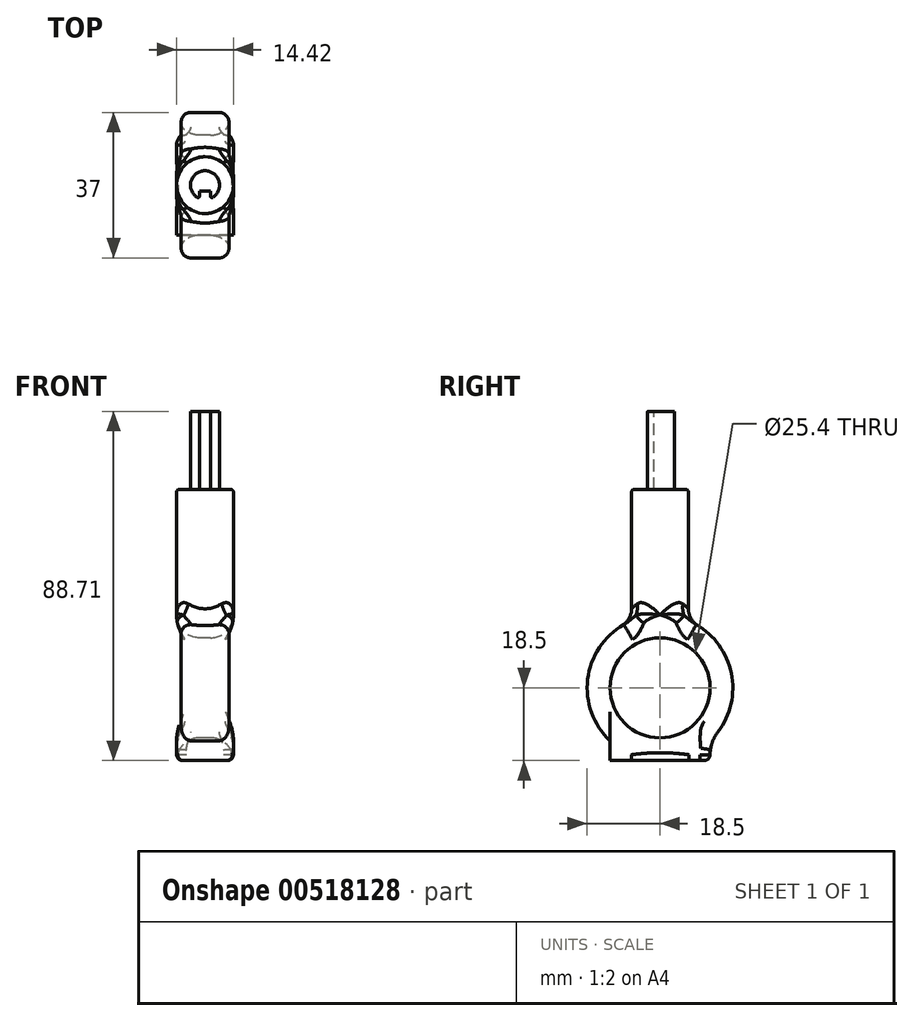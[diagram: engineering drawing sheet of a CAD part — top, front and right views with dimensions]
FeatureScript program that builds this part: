
annotation { "Feature Type Name" : "Feature", "Feature Type Description" : "" }
export const myFeature = defineFeature(function(context is Context, id is Id, definition is map)
    precondition{}
    {
        {
            var Q0;
            Q0=qCreatedBy(makeId("Top.planeOp"),FACE);
            var sketch = newSketch(context, id + "F0", { "sketchPlane" : qUnion([Q0])});
            skCircle(sketch, "E0", {"center": v(0, 0) * mm, "radius": 3.68 * mm});
            skSolve(sketch);
        }
        {
            var Q0;
            Q0 = qSketchRegion(id + "F0", true);
            extrude(context, id + "F1", {"entities" : qUnion([Q0]), "depth" : 19.8 * mm, "offsetDistance" : 25.4 * mm});
        }
        {
            var Q0;
            Q0=makeQuery(id+"F1.opExtrude","CAP_FACE",FACE,{"disambiguationData":[OSD([sQuery(id+"F0.wireOp",EDGE,"E0")])],"isStart":false});
            var sketch = newSketch(context, id + "F2", { "sketchPlane" : qUnion([Q0])});
            skLineSegment(sketch, "E1.bottom", {"start": v(-1.4, -3.68) * mm, "end": v(1.4, -3.68) * mm});
            skLineSegment(sketch, "E1.top", {"start": v(-1.4, -1.51) * mm, "end": v(1.4, -1.51) * mm});
            skLineSegment(sketch, "E1.left", {"start": v(-1.4, -3.68) * mm, "end": v(-1.4, -1.51) * mm});
            skLineSegment(sketch, "E1.right", {"start": v(1.4, -3.68) * mm, "end": v(1.4, -1.51) * mm});
            skSolve(sketch);
        }
        {
            var Q0;
            Q0 = qSketchRegion(id + "F2", true);
            extrude(context, id + "F3", {"entities" : qUnion([Q0]), "operationType" : NewBodyOperationType.REMOVE, "oppositeDirection" : true, "depth" : 25.4 * mm, "offsetDistance" : 25.4 * mm});
        }
        {
            var Q0;
            Q0=makeQuery(id+"F3.boolean.opBoolean","INTERSECT",EDGE,{"derivedFrom":[makeQuery(id+"F1.opExtrude","SWEPT_FACE",FACE,{"disambiguationData":[OSD([sQuery(id+"F0.wireOp",EDGE,"E0")])]}),makeQuery(id+"F3.opExtrude","SWEPT_FACE",FACE,{"disambiguationData":[OSD([sQuery(id+"F2.wireOp",EDGE,"E1.right")])]})]});
            var Q1;
            Q1=makeQuery(id+"F3.boolean.opBoolean","INTERSECT",EDGE,{"derivedFrom":[makeQuery(id+"F1.opExtrude","SWEPT_FACE",FACE,{"disambiguationData":[OSD([sQuery(id+"F0.wireOp",EDGE,"E0")])]}),makeQuery(id+"F3.opExtrude","SWEPT_FACE",FACE,{"disambiguationData":[OSD([sQuery(id+"F2.wireOp",EDGE,"E1.left")])]})]});
            fillet(context, id + "F4", {"entities" : qUnion([Q0, Q1]), "radius" : 0.38 * mm, "tangentPropagation" : true, "allowEdgeOverflow" : false});
        }
        {
            var Q0;
            Q0=makeQuery(id+"F1.opExtrude","CAP_FACE",FACE,{"disambiguationData":[OSD([sQuery(id+"F0.wireOp",EDGE,"E0")])],"isStart":true});
            var sketch = newSketch(context, id + "F5", { "sketchPlane" : qUnion([Q0])});
            skCircle(sketch, "E2", {"center": v(0, 0) * mm, "radius": 7.21 * mm});
            skSolve(sketch);
        }
        {
            var Q0;
            Q0 = qSketchRegion(id + "F5", true);
            extrude(context, id + "F6", {"entities" : qUnion([Q0]), "operationType" : NewBodyOperationType.ADD, "depth" : 12.7 * mm, "offsetDistance" : 25.4 * mm});
        }
        {
            var Q0;
            Q0=makeQuery(id+"F6.opExtrude","CAP_EDGE",EDGE,{"disambiguationData":[OSD([sQuery(id+"F5.wireOp",EDGE,"E2")])],"isStart":false});
            fillet(context, id + "F7", {"entities" : qUnion([Q0]), "radius" : 2.54 * mm, "tangentPropagation" : true, "allowEdgeOverflow" : false});
        }
        {
            var Q0;
            Q0=makeQuery(id+"F6.opExtrude","CAP_EDGE",EDGE,{"disambiguationData":[OSD([sQuery(id+"F5.wireOp",EDGE,"E2")])],"isStart":true});
            fillet(context, id + "F8", {"entities" : qUnion([Q0]), "radius" : 0.64 * mm, "tangentPropagation" : true, "allowEdgeOverflow" : false});
        }
        {
            var Q0;
            Q0=makeQuery(id+"F6.opExtrude","CAP_FACE",FACE,{"disambiguationData":[OSD([sQuery(id+"F5.wireOp",EDGE,"E2")])],"isStart":false});
            var sketch = newSketch(context, id + "F9", { "sketchPlane" : qUnion([Q0])});
            skCircle(sketch, "E3.0", {"center": v(0, 0) * mm, "radius": 7.21 * mm});
            skSolve(sketch);
        }
        {
            var Q0;
            Q0 = qSketchRegion(id + "F9", true);
            extrude(context, id + "F10", {"entities" : qUnion([Q0]), "operationType" : NewBodyOperationType.ADD, "depth" : 25 * mm, "offsetDistance" : 25 * mm, "hasSecondDirection" : true, "secondDirectionOppositeDirection" : true, "secondDirectionDepth" : 5 * mm});
        }
        {
            var Q0;
            Q0=qCreatedBy(makeId("Right.planeOp"),FACE);
            var sketch = newSketch(context, id + "F11", { "sketchPlane" : qUnion([Q0])});
            skCircle(sketch, "E4", {"center": v(0, -50.4) * mm, "radius": 12.7 * mm});
            skCircle(sketch, "E5", {"center": v(0, -50.4) * mm, "radius": 18.5 * mm});
            skSolve(sketch);
        }
        {
            var Q0;
            Q0 = qSketchRegion(id + "F11", true);
            extrude(context, id + "F12", {"entities" : qUnion([Q0]), "operationType" : NewBodyOperationType.ADD, "depth" : (14.43 / 2) * mm, "offsetDistance" : 25 * mm, "hasSecondDirection" : true, "secondDirectionOppositeDirection" : true, "secondDirectionDepth" : (14.43 / 2) * mm});
        }
        {
            var Q0;
            Q0=makeQuery(id+"F12.opExtrude","CAP_FACE",FACE,{"disambiguationData":[OSD([sQuery(id+"F11.wireOp",EDGE,"E4"),sQuery(id+"F11.wireOp",EDGE,"E5")])],"isStart":false});
            var sketch = newSketch(context, id + "F13", { "sketchPlane" : qUnion([Q0])});
            skLineSegment(sketch, "E6", {"start": v(-12.7, -63.85) * mm, "end": v(-12.7, -68.9) * mm});
            skLineSegment(sketch, "E7", {"start": v(-12.7, -68.9) * mm, "end": v(12.7, -68.9) * mm});
            skLineSegment(sketch, "E8", {"start": v(12.7, -68.9) * mm, "end": v(12.7, -63.85) * mm});
            skLineSegment(sketch, "E9", {"start": v(12.7, -63.85) * mm, "end": v(5.8, -66.43) * mm});
            skLineSegment(sketch, "E10", {"start": v(5.8, -66.43) * mm, "end": v(-3.07, -66.43) * mm});
            skLineSegment(sketch, "E11", {"start": v(-3.07, -66.43) * mm, "end": v(-12.7, -63.85) * mm});
            skSolve(sketch);
        }
        {
            var Q0;
            Q0 = qSketchRegion(id + "F13", true);
            var Q1;
            Q1=makeQuery(id+"F12.opExtrude","CAP_FACE",FACE,{"disambiguationData":[OSD([sQuery(id+"F11.wireOp",EDGE,"E4"),sQuery(id+"F11.wireOp",EDGE,"E5")])],"isStart":true});
            extrude(context, id + "F14", {"entities" : qUnion([Q0]), "operationType" : NewBodyOperationType.ADD, "endBound" : BoundingType.UP_TO_SURFACE, "oppositeDirection" : true, "depth" : 14.43 * mm, "endBoundEntityFace" : qUnion([Q1]), "offsetDistance" : 25 * mm});
        }
        {
            var Q0;
            Q0=makeQuery(id+"F14.opExtrude","SWEPT_EDGE",EDGE,{"disambiguationData":[OSD([sQuery(id+"F11.wireOp",EDGE,"E5"),sQuery(id+"F13.wireOp",EDGE,"E8"),sQuery(id+"F13.wireOp",EDGE,"E9")])]});
            var Q1;
            Q1=makeQuery(id+"F14.opExtrude","SWEPT_EDGE",EDGE,{"disambiguationData":[OSD([sQuery(id+"F11.wireOp",EDGE,"E5"),sQuery(id+"F13.wireOp",EDGE,"E6"),sQuery(id+"F13.wireOp",EDGE,"E11")])]});
            fillet(context, id + "F15", {"entities" : qUnion([Q0, Q1]), "tangentPropagation" : true, "radius" : 10 * mm, "defaultsChanged" : true, "vertexSettings" : [], "allowEdgeOverflow" : false});
        }
        {
            var Q0;
            Q0=makeQuery(id+"F12.opExtrude","CAP_EDGE",EDGE,{"disambiguationData":[OSD([sQuery(id+"F11.wireOp",EDGE,"E4")])],"isStart":false});
            fillet(context, id + "F16", {"entities" : qUnion([Q0]), "tangentPropagation" : true, "radius" : 5.8 * mm, "defaultsChanged" : true, "vertexSettings" : [], "allowEdgeOverflow" : false});
        }
        {
            var Q0;
            Q0=makeQuery(id+"F12.opExtrude","CAP_EDGE",EDGE,{"disambiguationData":[OSD([sQuery(id+"F11.wireOp",EDGE,"E4")])],"isStart":true});
            fillet(context, id + "F17", {"entities" : qUnion([Q0]), "tangentPropagation" : true, "radius" : 5.8 * mm, "defaultsChanged" : true, "vertexSettings" : [], "allowEdgeOverflow" : false});
        }
        {
            var Q0;
            Q0=makeQuery(id+"F12.boolean.opBoolean","INTERSECT",EDGE,{"disambiguationData":[OD(0.0)],"derivedFrom":[makeQuery(id+"F10.boolean.opBoolean","MERGE",FACE,{"derivedFrom":[makeQuery(id+"F6.opExtrude","SWEPT_FACE",FACE,{"disambiguationData":[OSD([sQuery(id+"F5.wireOp",EDGE,"E2")])]}),makeQuery(id+"F10.opExtrude","SWEPT_FACE",FACE,{"disambiguationData":[OSD([sQuery(id+"F9.wireOp",EDGE,"E3.0")])]})]}),makeQuery(id+"F12.opExtrude","SWEPT_FACE",FACE,{"disambiguationData":[OSD([sQuery(id+"F11.wireOp",EDGE,"E5")])]})]});
            fillet(context, id + "F18", {"entities" : qUnion([Q0]), "tangentPropagation" : true, "radius" : 5 * mm, "defaultsChanged" : false, "vertexSettings" : [], "allowEdgeOverflow" : false});
        }
        {
            var Q0;
            {var subQ0=sQuery(id+"F11.wireOp",EDGE,"E5");var subQ1=sQuery(id+"F11.wireOp",EDGE,"E4");var subQ7=sQuery(id+"F13.wireOp",EDGE,"E6");var subQ8=makeQuery(id+"F12.opExtrude","SWEPT_FACE",FACE,{"disambiguationData":[OSD([subQ0])]});Q0=makeQuery(id+"F16.opFillet","BLEND_EDGE",EDGE,{"blendedFrom":[makeQuery(id+"F12.opExtrude","CAP_EDGE",EDGE,{"disambiguationData":[OSD([subQ1])],"isStart":false}),makeQuery(id+"F14.boolean.opBoolean","SPLIT",FACE,{"disambiguationData":[TD([makeQuery(id+"F14.opExtrude","SWEPT_FACE",FACE,{"disambiguationData":[OSD([subQ7])]})])],"derivedFrom":subQ8})],"blendedInto":[makeQuery(id+"F14.boolean.opBoolean","SPLIT",FACE,{"disambiguationData":[TD([makeQuery(id+"F14.opExtrude","SWEPT_FACE",FACE,{"disambiguationData":[OSD([subQ7])]})])],"derivedFrom":subQ8})]});}
            var Q1;
            {var subQ0=sQuery(id+"F11.wireOp",EDGE,"E5");var subQ1=sQuery(id+"F11.wireOp",EDGE,"E4");var subQ5=sQuery(id+"F13.wireOp",EDGE,"E8");var subQ8=makeQuery(id+"F12.opExtrude","SWEPT_FACE",FACE,{"disambiguationData":[OSD([subQ0])]});Q1=makeQuery(id+"F16.opFillet","BLEND_EDGE",EDGE,{"blendedFrom":[makeQuery(id+"F12.opExtrude","CAP_EDGE",EDGE,{"disambiguationData":[OSD([subQ1])],"isStart":false}),makeQuery(id+"F14.boolean.opBoolean","SPLIT",FACE,{"disambiguationData":[TD([makeQuery(id+"F14.opExtrude","SWEPT_FACE",FACE,{"disambiguationData":[OSD([subQ5])]})])],"derivedFrom":subQ8})],"blendedInto":[makeQuery(id+"F14.boolean.opBoolean","SPLIT",FACE,{"disambiguationData":[TD([makeQuery(id+"F14.opExtrude","SWEPT_FACE",FACE,{"disambiguationData":[OSD([subQ5])]})])],"derivedFrom":subQ8})]});}
            var Q2;
            {var subQ0=sQuery(id+"F11.wireOp",EDGE,"E5");var subQ1=sQuery(id+"F11.wireOp",EDGE,"E4");var subQ7=sQuery(id+"F13.wireOp",EDGE,"E6");var subQ8=makeQuery(id+"F12.opExtrude","SWEPT_FACE",FACE,{"disambiguationData":[OSD([subQ0])]});Q2=makeQuery(id+"F17.opFillet","BLEND_EDGE",EDGE,{"blendedFrom":[makeQuery(id+"F12.opExtrude","CAP_EDGE",EDGE,{"disambiguationData":[OSD([subQ1])],"isStart":true}),makeQuery(id+"F14.boolean.opBoolean","SPLIT",FACE,{"disambiguationData":[TD([makeQuery(id+"F14.opExtrude","SWEPT_FACE",FACE,{"disambiguationData":[OSD([subQ7])]})])],"derivedFrom":subQ8})],"blendedInto":[makeQuery(id+"F14.boolean.opBoolean","SPLIT",FACE,{"disambiguationData":[TD([makeQuery(id+"F14.opExtrude","SWEPT_FACE",FACE,{"disambiguationData":[OSD([subQ7])]})])],"derivedFrom":subQ8})]});}
            var Q3;
            {var subQ0=sQuery(id+"F11.wireOp",EDGE,"E5");var subQ1=sQuery(id+"F11.wireOp",EDGE,"E4");var subQ5=sQuery(id+"F13.wireOp",EDGE,"E8");var subQ8=makeQuery(id+"F12.opExtrude","SWEPT_FACE",FACE,{"disambiguationData":[OSD([subQ0])]});Q3=makeQuery(id+"F17.opFillet","BLEND_EDGE",EDGE,{"blendedFrom":[makeQuery(id+"F12.opExtrude","CAP_EDGE",EDGE,{"disambiguationData":[OSD([subQ1])],"isStart":true}),makeQuery(id+"F14.boolean.opBoolean","SPLIT",FACE,{"disambiguationData":[TD([makeQuery(id+"F14.opExtrude","SWEPT_FACE",FACE,{"disambiguationData":[OSD([subQ5])]})])],"derivedFrom":subQ8})],"blendedInto":[makeQuery(id+"F14.boolean.opBoolean","SPLIT",FACE,{"disambiguationData":[TD([makeQuery(id+"F14.opExtrude","SWEPT_FACE",FACE,{"disambiguationData":[OSD([subQ5])]})])],"derivedFrom":subQ8})]});}
            fillet(context, id + "F19", {"entities" : qUnion([Q0, Q1, Q2, Q3]), "tangentPropagation" : true, "radius" : 2.5 * mm, "defaultsChanged" : false, "vertexSettings" : [], "allowEdgeOverflow" : false});
        }
        {
            var Q0;
            Q0=makeQuery(id+"F14.opExtrude","CAP_EDGE",EDGE,{"disambiguationData":[OSD([sQuery(id+"F13.wireOp",EDGE,"E7")])],"isStart":true});
            fillet(context, id + "F20", {"entities" : qUnion([Q0]), "tangentPropagation" : true, "radius" : 1.5 * mm, "defaultsChanged" : true, "vertexSettings" : [], "allowEdgeOverflow" : false});
        }
    });
